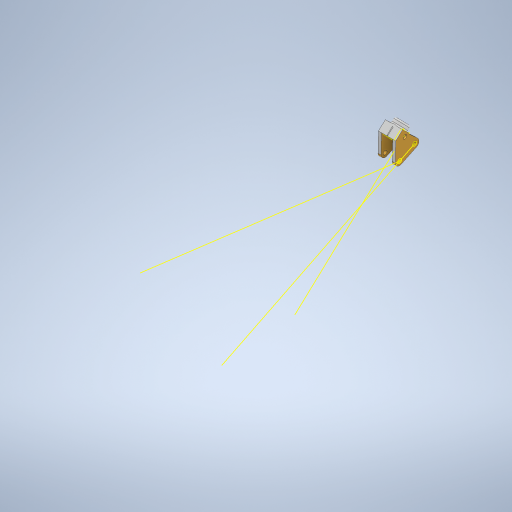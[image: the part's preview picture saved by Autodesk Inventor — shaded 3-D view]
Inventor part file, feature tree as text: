
AUTODESK INVENTOR PART (.ipt)
format: ipt  version: 2023 (Build 270158000, 158)  size: 471,040 bytes
history: native  units: mm
features: sketch x9, other x4, projected_geometry x4, extrude x3
ambient origin geometry x8: Origin, YZ Plane, XZ Plane, XY Plane, X Axis, Y Axis, Z Axis, Center Point
bodies: Solid2 (feature_tree)
feature tree (20):
  other  "preadator nano fixed mount template.iam"
  other  "Kauri modular camera mount HDzero micro v1 mirror.ipt:1"
  other  "Kauri modular camera mount HDzero micro v1.ipt:1"
  other  "camera housing V1.ipt:1"
  extrude  "Extrusion1"  Depth=10.0mm TaperAngle=0.0deg
  extrude  "Extrusion2"  Depth=0.5mm
  extrude  "Extrusion3"  Depth=10.0mm TaperAngle=0.0deg
  sketch  "Sketch15"
  sketch  "Sketch1"  dims[d1=10.0mm d2=10.0mm d3=0.0mm]
  sketch  "Sketch1_1"  dims[d4=10.0mm d5=0.0mm d6=0.5mm]
  sketch  "Sketch6"  dims[d10=2.871067mm]
  sketch  "Sketch11"
  sketch  "Sketch10"
  projected_geometry  "Projected Loop3"
  sketch  "Sketch12"
  projected_geometry  "Projected Loop4"
  projected_geometry  "Projected Loop5"
  sketch  "Sketch13"
  projected_geometry  "Projected Loop6"
  sketch  "Sketch10_1"  dims[d7=0.5mm d8=10.0mm d9=0.0mm]
